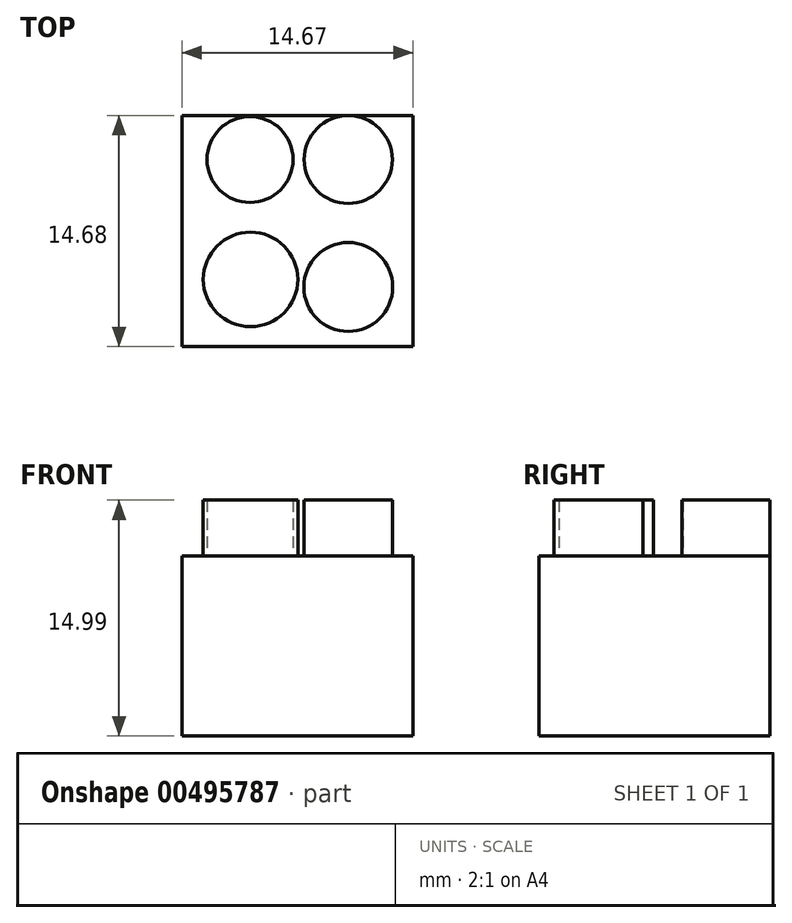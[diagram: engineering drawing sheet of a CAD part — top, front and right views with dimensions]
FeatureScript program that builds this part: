
annotation { "Feature Type Name" : "Feature", "Feature Type Description" : "" }
export const myFeature = defineFeature(function(context is Context, id is Id, definition is map)
    precondition{}
    {
        {
            var Q0;
            Q0=qCreatedBy(makeId("Top.planeOp"),FACE);
            var sketch = newSketch(context, id + "F0", { "sketchPlane" : qUnion([Q0])});
            skLineSegment(sketch, "E0.bottom", {"start": v(-188.81, -71.78) * mm, "end": v(-174.14, -71.78) * mm});
            skLineSegment(sketch, "E0.top", {"start": v(-188.81, -86.46) * mm, "end": v(-174.14, -86.46) * mm});
            skLineSegment(sketch, "E0.left", {"start": v(-188.81, -71.78) * mm, "end": v(-188.81, -86.46) * mm});
            skLineSegment(sketch, "E0.right", {"start": v(-174.14, -71.78) * mm, "end": v(-174.14, -86.46) * mm});
            skSolve(sketch);
        }
        {
            var Q0;
            Q0=makeQuery(id+"F0.imprint","IMPRINT",FACE,{"disambiguationData":[TD([[makeQuery(id+"F0.imprint","IMPRINT",EDGE,{"derivedFrom":sQuery(id+"F0.wireOp",EDGE,"E0.bottom")}),-1.0]])]});
            var sketch = newSketch(context, id + "F1", { "sketchPlane" : qUnion([Q0])});
            skSolve(sketch);
        }
        {
            var Q0;
            Q0=makeQuery(id+"F1.imprint","IMPRINT",FACE,{"disambiguationData":[TD([[makeQuery(id+"F1.imprint","IMPRINT",EDGE,{"derivedFrom":makeQuery(id+"F0.imprint","IMPRINT",EDGE,{"derivedFrom":sQuery(id+"F0.wireOp",EDGE,"E0.bottom")})}),-1.0]])]});
            extrude(context, id + "F2", {"entities" : qUnion([Q0]), "depth" : 11.43 * mm});
        }
        {
            var Q0;
            Q0=makeQuery(id+"F2.opExtrude","CAP_FACE",FACE,{"disambiguationData":[OSD([sQuery(id+"F0.wireOp",EDGE,"E0.bottom"),sQuery(id+"F0.wireOp",EDGE,"E0.top"),sQuery(id+"F0.wireOp",EDGE,"E0.left"),sQuery(id+"F0.wireOp",EDGE,"E0.right")])],"isStart":false});
            var sketch = newSketch(context, id + "F3", { "sketchPlane" : qUnion([Q0])});
            skCircle(sketch, "E1", {"center": v(-178.25, -74.58) * mm, "radius": 2.8 * mm});
            skCircle(sketch, "E2", {"center": v(-178.25, -82.68) * mm, "radius": 2.82 * mm});
            skCircle(sketch, "E3", {"center": v(-184.5, -74.58) * mm, "radius": 2.73 * mm});
            skCircle(sketch, "E4", {"center": v(-184.46, -82.2) * mm, "radius": 3 * mm});
            skSolve(sketch);
        }
        {
            var Q0;
            Q0=makeQuery(id+"F3.imprint","IMPRINT",FACE,{"disambiguationData":[TD([[makeQuery(id+"F3.imprint","IMPRINT",EDGE,{"derivedFrom":sQuery(id+"F3.wireOp",EDGE,"E1")}),1.0]])]});
            var sketch = newSketch(context, id + "F4", { "sketchPlane" : qUnion([Q0])});
            skSolve(sketch);
        }
        {
            var Q0;
            Q0 = qSketchRegion(id + "F4", true);
            var Q1;
            Q1=makeQuery(id+"F3.imprint","IMPRINT",FACE,{"disambiguationData":[TD([[makeQuery(id+"F3.imprint","IMPRINT",EDGE,{"derivedFrom":sQuery(id+"F3.wireOp",EDGE,"E1")}),1.0]])]});
            var Q2;
            Q2=makeQuery(id+"F3.imprint","IMPRINT",FACE,{"disambiguationData":[TD([[makeQuery(id+"F3.imprint","IMPRINT",EDGE,{"derivedFrom":sQuery(id+"F3.wireOp",EDGE,"E2")}),1.0]])]});
            var Q3;
            Q3=makeQuery(id+"F3.imprint","IMPRINT",FACE,{"disambiguationData":[TD([[makeQuery(id+"F3.imprint","IMPRINT",EDGE,{"derivedFrom":sQuery(id+"F3.wireOp",EDGE,"E3")}),1.0]])]});
            var Q4;
            Q4=makeQuery(id+"F3.imprint","IMPRINT",FACE,{"disambiguationData":[TD([[makeQuery(id+"F3.imprint","IMPRINT",EDGE,{"derivedFrom":sQuery(id+"F3.wireOp",EDGE,"E4")}),1.0]])]});
            extrude(context, id + "F5", {"entities" : qUnion([Q0, Q1, Q2, Q3, Q4]), "operationType" : NewBodyOperationType.ADD, "depth" : 3.56 * mm});
        }
    });
